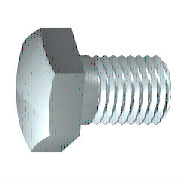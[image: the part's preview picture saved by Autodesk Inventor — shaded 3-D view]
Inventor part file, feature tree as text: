
AUTODESK INVENTOR PART (.ipt)
format: ipt  version: 2020 (Build 240168000, 168)  size: 195,584 bytes
history: native  units: mm (DEFAULTED — no unit token found)
features: sketch x3, extrude x1, chamfer x1, plane x1
ambient origin geometry x7: Origin, YZ Plane, XZ Plane, X Axis, Y Axis, Z Axis, Center Point
bodies: Solid1 (feature_tree), Body (feature_tree)
feature tree (6):
  extrude  "Head"  Depth=51.25mm
  chamfer  "Chamfer1"  Distance=4.7mm
  plane  "Work Plane1"
  sketch  "Sketch1"  dims[d0=55.0mm d1=51.25mm]
  sketch  "Sketch2"  dims[d2=8.0mm]
  sketch  "Sketch4"  dims[d12=90.0deg d3=4.7mm d4=0.0mm d5=30.0deg d21=90.0deg d6=0.766813mm d7=0.766912mm d8=0.0mm d9=0.6001mm d10=11.4mm d11=13.0mm d13=0.766912mm d14=7.323417mm d15=51.25mm d16=0.0mm d19=13.0mm d55=45.0deg d57=0.0mm d58=0.0mm]
